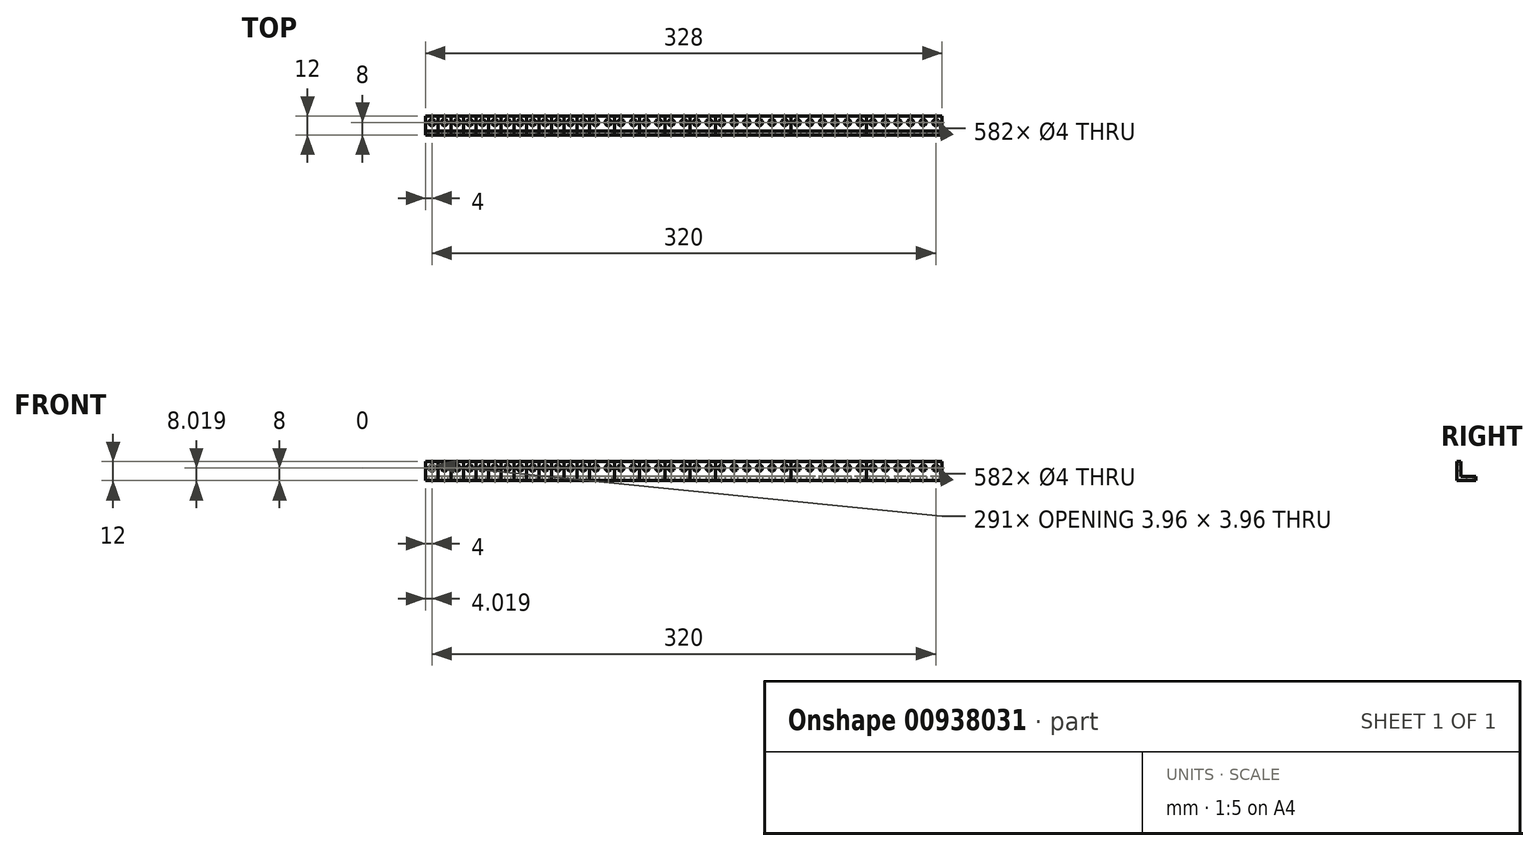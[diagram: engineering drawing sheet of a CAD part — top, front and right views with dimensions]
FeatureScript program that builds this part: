
annotation { "Feature Type Name" : "Feature", "Feature Type Description" : "" }
export const myFeature = defineFeature(function(context is Context, id is Id, definition is map)
    precondition{}
    {
        {
            var Q0;
            Q0=qCreatedBy(makeId("Right.planeOp"),FACE);
            var sketch = newSketch(context, id + "F0", { "sketchPlane" : qUnion([Q0]) });
            skLineSegment(sketch, "E0.bottom", {"start": v(0, 0) * mm, "end": v(12, 0) * mm});
            skLineSegment(sketch, "E0.top", {"start": v(0, 12) * mm, "end": v(2.5, 12) * mm});
            skLineSegment(sketch, "E0.left", {"start": v(0, 0) * mm, "end": v(0, 12) * mm});
            skLineSegment(sketch, "E1.left", {"start": v(2.5, 12) * mm, "end": v(2.5, 2.5) * mm});
            skLineSegment(sketch, "E2", {"start": v(12, 0) * mm, "end": v(12, 2.5) * mm});
            skLineSegment(sketch, "E3", {"start": v(2.5, 2.5) * mm, "end": v(12, 2.5) * mm});
            skSolve(sketch);
        }
        {
            var Q0;
            Q0=qSketchRegion(id+"F0",true);
            extrude(context, id + "F1", {"entities" : qUnion([Q0]), "depth" : 8 * mm, "offsetDistance" : 25 * mm});
        }
        {
            var Q0;
            Q0=qSketchRegion(id+"F0",true);
            extrude(context, id + "F2", {"entities" : qUnion([Q0]), "depth" : 16 * mm, "offsetDistance" : 25 * mm});
        }
        {
            var Q0;
            Q0=qSketchRegion(id+"F0",true);
            extrude(context, id + "F3", {"entities" : qUnion([Q0]), "depth" : 24 * mm, "offsetDistance" : 25 * mm});
        }
        {
            var Q0;
            Q0=qSketchRegion(id+"F0",true);
            extrude(context, id + "F4", {"entities" : qUnion([Q0]), "depth" : 32 * mm, "offsetDistance" : 25 * mm});
        }
        {
            var Q0;
            Q0=qSketchRegion(id+"F0",true);
            extrude(context, id + "F5", {"entities" : qUnion([Q0]), "depth" : 40 * mm, "offsetDistance" : 25 * mm});
        }
        {
            var Q0;
            Q0=qSketchRegion(id+"F0",true);
            extrude(context, id + "F6", {"entities" : qUnion([Q0]), "depth" : 48 * mm, "offsetDistance" : 25 * mm});
        }
        {
            var Q0;
            Q0=qSketchRegion(id+"F0",true);
            extrude(context, id + "F7", {"entities" : qUnion([Q0]), "depth" : 56 * mm, "offsetDistance" : 25 * mm});
        }
        {
            var Q0;
            Q0=qSketchRegion(id+"F0",true);
            extrude(context, id + "F8", {"entities" : qUnion([Q0]), "depth" : 64 * mm, "offsetDistance" : 25 * mm});
        }
        {
            var Q0;
            Q0=qSketchRegion(id+"F0",true);
            extrude(context, id + "F9", {"entities" : qUnion([Q0]), "depth" : 72 * mm, "offsetDistance" : 25 * mm});
        }
        {
            var Q0;
            Q0=qSketchRegion(id+"F0",true);
            extrude(context, id + "F10", {"entities" : qUnion([Q0]), "depth" : 80 * mm, "offsetDistance" : 25 * mm});
        }
        {
            var Q0;
            Q0=qSketchRegion(id+"F0",true);
            extrude(context, id + "F11", {"entities" : qUnion([Q0]), "depth" : 88 * mm, "offsetDistance" : 25 * mm});
        }
        {
            var Q0;
            Q0=qSketchRegion(id+"F0",true);
            extrude(context, id + "F12", {"entities" : qUnion([Q0]), "depth" : 96 * mm, "offsetDistance" : 25 * mm});
        }
        {
            var Q0;
            Q0=qSketchRegion(id+"F0",true);
            extrude(context, id + "F13", {"entities" : qUnion([Q0]), "depth" : 104 * mm, "offsetDistance" : 25 * mm});
        }
        {
            var Q0;
            Q0=qSketchRegion(id+"F0",true);
            extrude(context, id + "F14", {"entities" : qUnion([Q0]), "depth" : 120 * mm, "offsetDistance" : 25 * mm});
        }
        {
            var Q0;
            Q0=qSketchRegion(id+"F0",true);
            extrude(context, id + "F15", {"entities" : qUnion([Q0]), "depth" : 136 * mm, "offsetDistance" : 25 * mm});
        }
        {
            var Q0;
            Q0=qSketchRegion(id+"F0",true);
            extrude(context, id + "F16", {"entities" : qUnion([Q0]), "depth" : 152 * mm, "offsetDistance" : 25 * mm});
        }
        {
            var Q0;
            Q0=qSketchRegion(id+"F0",true);
            extrude(context, id + "F17", {"entities" : qUnion([Q0]), "depth" : 168 * mm, "offsetDistance" : 25 * mm});
        }
        {
            var Q0;
            Q0=qSketchRegion(id+"F0",true);
            extrude(context, id + "F18", {"entities" : qUnion([Q0]), "depth" : 184 * mm, "offsetDistance" : 25 * mm});
        }
        {
            var Q0;
            Q0=qSketchRegion(id+"F0",true);
            extrude(context, id + "F19", {"entities" : qUnion([Q0]), "depth" : 232 * mm, "offsetDistance" : 25 * mm});
        }
        {
            var Q0;
            Q0=qSketchRegion(id+"F0",true);
            extrude(context, id + "F20", {"entities" : qUnion([Q0]), "depth" : 280 * mm, "offsetDistance" : 25 * mm});
        }
        {
            var Q0;
            Q0=qSketchRegion(id+"F0",true);
            extrude(context, id + "F21", {"entities" : qUnion([Q0]), "depth" : 328 * mm, "offsetDistance" : 25 * mm});
        }
        {
            var Q0;
            Q0=qCreatedBy(makeId("Front.planeOp"),FACE);
            var sketch = newSketch(context, id + "F22", { "sketchPlane" : qUnion([Q0]) });
            skLineSegment(sketch, "E4.bottom", {"start": v(0, 0) * mm, "end": v(4, 0) * mm, "construction": true});
            skLineSegment(sketch, "E4.top", {"start": v(0, 8) * mm, "end": v(4, 8) * mm, "construction": true});
            skLineSegment(sketch, "E4.left", {"start": v(0, 0) * mm, "end": v(0, 8) * mm, "construction": true});
            skLineSegment(sketch, "E4.right", {"start": v(4, 0) * mm, "end": v(4, 8) * mm, "construction": true});
            skCircle(sketch, "E5", {"center": v(4, 8) * mm, "radius": 2 * mm});
            skCircle(sketch, "E6.1.0.0", {"center": v(12, 8) * mm, "radius": 2 * mm});
            skCircle(sketch, "E6.2.0.0", {"center": v(20, 8) * mm, "radius": 2 * mm});
            skLineSegment(sketch, "E6.direction1", {"start": v(4, 8) * mm, "end": v(12, 8) * mm, "construction": true});
            skCircle(sketch, "E7.0.3.0", {"center": v(28, 8) * mm, "radius": 2 * mm});
            skCircle(sketch, "E7.0.4.0", {"center": v(36, 8) * mm, "radius": 2 * mm});
            skCircle(sketch, "E7.0.5.0", {"center": v(44, 8) * mm, "radius": 2 * mm});
            skCircle(sketch, "E7.0.6.0", {"center": v(52, 8) * mm, "radius": 2 * mm});
            skCircle(sketch, "E7.0.7.0", {"center": v(60, 8) * mm, "radius": 2 * mm});
            skCircle(sketch, "E7.0.8.0", {"center": v(68, 8) * mm, "radius": 2 * mm});
            skCircle(sketch, "E7.0.9.0", {"center": v(76, 8) * mm, "radius": 2 * mm});
            skCircle(sketch, "E7.0.10.0", {"center": v(84, 8) * mm, "radius": 2 * mm});
            skCircle(sketch, "E7.0.11.0", {"center": v(92, 8) * mm, "radius": 2 * mm});
            skCircle(sketch, "E7.0.12.0", {"center": v(100, 8) * mm, "radius": 2 * mm});
            skCircle(sketch, "E7.0.13.0", {"center": v(108, 8) * mm, "radius": 2 * mm});
            skCircle(sketch, "E7.0.14.0", {"center": v(116, 8) * mm, "radius": 2 * mm});
            skCircle(sketch, "E7.0.15.0", {"center": v(124, 8) * mm, "radius": 2 * mm});
            skCircle(sketch, "E7.0.16.0", {"center": v(132, 8) * mm, "radius": 2 * mm});
            skCircle(sketch, "E7.0.17.0", {"center": v(140, 8) * mm, "radius": 2 * mm});
            skCircle(sketch, "E7.0.18.0", {"center": v(148, 8) * mm, "radius": 2 * mm});
            skCircle(sketch, "E7.0.19.0", {"center": v(156, 8) * mm, "radius": 2 * mm});
            skCircle(sketch, "E7.0.20.0", {"center": v(164, 8) * mm, "radius": 2 * mm});
            skCircle(sketch, "E7.0.21.0", {"center": v(172, 8) * mm, "radius": 2 * mm});
            skCircle(sketch, "E7.0.22.0", {"center": v(180, 8) * mm, "radius": 2 * mm});
            skCircle(sketch, "E7.0.23.0", {"center": v(188, 8) * mm, "radius": 2 * mm});
            skCircle(sketch, "E7.0.24.0", {"center": v(196, 8) * mm, "radius": 2 * mm});
            skCircle(sketch, "E7.0.25.0", {"center": v(204, 8) * mm, "radius": 2 * mm});
            skCircle(sketch, "E7.0.26.0", {"center": v(212, 8) * mm, "radius": 2 * mm});
            skCircle(sketch, "E7.0.27.0", {"center": v(220, 8) * mm, "radius": 2 * mm});
            skCircle(sketch, "E7.0.28.0", {"center": v(228, 8) * mm, "radius": 2 * mm});
            skCircle(sketch, "E7.0.29.0", {"center": v(236, 8) * mm, "radius": 2 * mm});
            skCircle(sketch, "E7.0.30.0", {"center": v(244, 8) * mm, "radius": 2 * mm});
            skCircle(sketch, "E7.0.31.0", {"center": v(252, 8) * mm, "radius": 2 * mm});
            skCircle(sketch, "E7.0.32.0", {"center": v(260, 8) * mm, "radius": 2 * mm});
            skCircle(sketch, "E7.0.33.0", {"center": v(268, 8) * mm, "radius": 2 * mm});
            skCircle(sketch, "E7.0.34.0", {"center": v(276, 8) * mm, "radius": 2 * mm});
            skCircle(sketch, "E7.0.35.0", {"center": v(284, 8) * mm, "radius": 2 * mm});
            skCircle(sketch, "E7.0.36.0", {"center": v(292, 8) * mm, "radius": 2 * mm});
            skCircle(sketch, "E7.0.37.0", {"center": v(300, 8) * mm, "radius": 2 * mm});
            skCircle(sketch, "E7.0.38.0", {"center": v(308, 8) * mm, "radius": 2 * mm});
            skCircle(sketch, "E7.0.39.0", {"center": v(316, 8) * mm, "radius": 2 * mm});
            skCircle(sketch, "E7.0.40.0", {"center": v(324, 8) * mm, "radius": 2 * mm});
            skSolve(sketch);
        }
        {
            var Q0;
            Q0=qSketchRegion(id+"F22",true);
            extrude(context, id + "F23", {"entities" : qUnion([Q0]), "operationType" : NewBodyOperationType.REMOVE, "endBound" : BoundingType.THROUGH_ALL, "oppositeDirection" : true, "depth" : 25 * mm, "offsetDistance" : 25 * mm});
        }
        {
            var Q0;
            Q0=qCreatedBy(makeId("Top.planeOp"),FACE);
            var sketch = newSketch(context, id + "F24", { "sketchPlane" : qUnion([Q0]) });
            skPoint(sketch, "E8.0", {"position": v(0, 12) * mm});
            skLineSegment(sketch, "E9.top", {"start": v(0, 0) * mm, "end": v(4, 0) * mm, "construction": true});
            skLineSegment(sketch, "E9.right", {"start": v(4, 8) * mm, "end": v(4, 0) * mm, "construction": true});
            skCircle(sketch, "E10", {"center": v(4, 8) * mm, "radius": 2 * mm});
            skCircle(sketch, "E11.1.0.0", {"center": v(12, 8) * mm, "radius": 2 * mm});
            skCircle(sketch, "E11.2.0.0", {"center": v(20, 8) * mm, "radius": 2 * mm});
            skCircle(sketch, "E11.3.0.0", {"center": v(28, 8) * mm, "radius": 2 * mm});
            skCircle(sketch, "E11.4.0.0", {"center": v(36, 8) * mm, "radius": 2 * mm});
            skCircle(sketch, "E11.5.0.0", {"center": v(44, 8) * mm, "radius": 2 * mm});
            skCircle(sketch, "E11.6.0.0", {"center": v(52, 8) * mm, "radius": 2 * mm});
            skCircle(sketch, "E11.7.0.0", {"center": v(60, 8) * mm, "radius": 2 * mm});
            skCircle(sketch, "E11.8.0.0", {"center": v(68, 8) * mm, "radius": 2 * mm});
            skCircle(sketch, "E11.9.0.0", {"center": v(76, 8) * mm, "radius": 2 * mm});
            skCircle(sketch, "E11.10.0.0", {"center": v(84, 8) * mm, "radius": 2 * mm});
            skCircle(sketch, "E11.11.0.0", {"center": v(92, 8) * mm, "radius": 2 * mm});
            skCircle(sketch, "E11.12.0.0", {"center": v(100, 8) * mm, "radius": 2 * mm});
            skCircle(sketch, "E11.13.0.0", {"center": v(108, 8) * mm, "radius": 2 * mm});
            skCircle(sketch, "E11.14.0.0", {"center": v(116, 8) * mm, "radius": 2 * mm});
            skCircle(sketch, "E11.15.0.0", {"center": v(124, 8) * mm, "radius": 2 * mm});
            skCircle(sketch, "E11.16.0.0", {"center": v(132, 8) * mm, "radius": 2 * mm});
            skCircle(sketch, "E11.17.0.0", {"center": v(140, 8) * mm, "radius": 2 * mm});
            skCircle(sketch, "E11.18.0.0", {"center": v(148, 8) * mm, "radius": 2 * mm});
            skCircle(sketch, "E11.19.0.0", {"center": v(156, 8) * mm, "radius": 2 * mm});
            skCircle(sketch, "E11.20.0.0", {"center": v(164, 8) * mm, "radius": 2 * mm});
            skCircle(sketch, "E11.21.0.0", {"center": v(172, 8) * mm, "radius": 2 * mm});
            skCircle(sketch, "E11.22.0.0", {"center": v(180, 8) * mm, "radius": 2 * mm});
            skCircle(sketch, "E11.23.0.0", {"center": v(188, 8) * mm, "radius": 2 * mm});
            skCircle(sketch, "E11.24.0.0", {"center": v(196, 8) * mm, "radius": 2 * mm});
            skCircle(sketch, "E11.25.0.0", {"center": v(204, 8) * mm, "radius": 2 * mm});
            skCircle(sketch, "E11.26.0.0", {"center": v(212, 8) * mm, "radius": 2 * mm});
            skCircle(sketch, "E11.27.0.0", {"center": v(220, 8) * mm, "radius": 2 * mm});
            skCircle(sketch, "E11.28.0.0", {"center": v(228, 8) * mm, "radius": 2 * mm});
            skCircle(sketch, "E11.29.0.0", {"center": v(236, 8) * mm, "radius": 2 * mm});
            skCircle(sketch, "E11.30.0.0", {"center": v(244, 8) * mm, "radius": 2 * mm});
            skCircle(sketch, "E11.31.0.0", {"center": v(252, 8) * mm, "radius": 2 * mm});
            skCircle(sketch, "E11.32.0.0", {"center": v(260, 8) * mm, "radius": 2 * mm});
            skCircle(sketch, "E11.33.0.0", {"center": v(268, 8) * mm, "radius": 2 * mm});
            skCircle(sketch, "E11.34.0.0", {"center": v(276, 8) * mm, "radius": 2 * mm});
            skCircle(sketch, "E11.35.0.0", {"center": v(284, 8) * mm, "radius": 2 * mm});
            skCircle(sketch, "E11.36.0.0", {"center": v(292, 8) * mm, "radius": 2 * mm});
            skCircle(sketch, "E11.37.0.0", {"center": v(300, 8) * mm, "radius": 2 * mm});
            skCircle(sketch, "E11.38.0.0", {"center": v(308, 8) * mm, "radius": 2 * mm});
            skCircle(sketch, "E11.39.0.0", {"center": v(316, 8) * mm, "radius": 2 * mm});
            skCircle(sketch, "E11.40.0.0", {"center": v(324, 8) * mm, "radius": 2 * mm});
            skLineSegment(sketch, "E11.direction1", {"start": v(4, 8) * mm, "end": v(12, 8) * mm, "construction": true});
            skPoint(sketch, "E12.orphan", {"position": v(4, 16) * mm});
            skSolve(sketch);
        }
        {
            var Q0;
            Q0=qSketchRegion(id+"F24",true);
            extrude(context, id + "F25", {"entities" : qUnion([Q0]), "operationType" : NewBodyOperationType.REMOVE, "endBound" : BoundingType.THROUGH_ALL, "depth" : 25 * mm, "offsetDistance" : 25 * mm});
        }
    });
